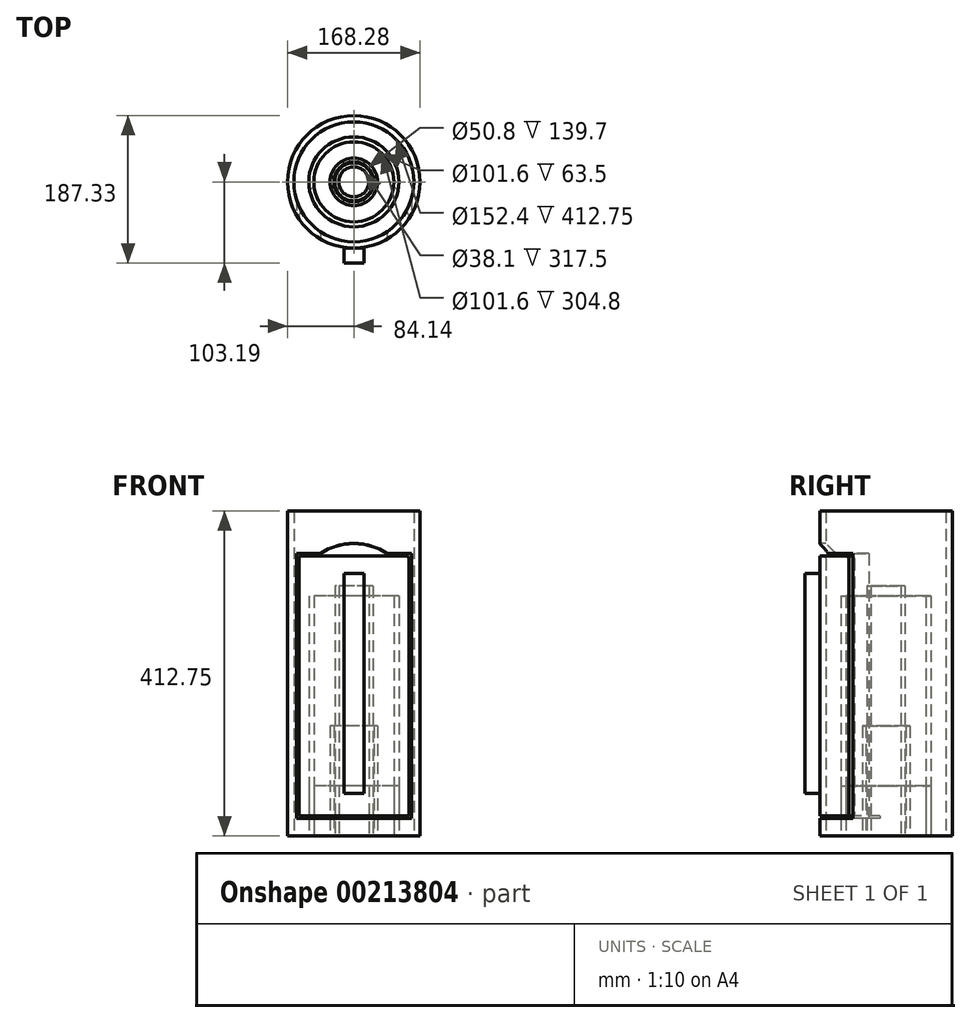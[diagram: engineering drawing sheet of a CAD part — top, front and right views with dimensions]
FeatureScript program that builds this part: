
annotation { "Feature Type Name" : "Feature", "Feature Type Description" : "" }
export const myFeature = defineFeature(function(context is Context, id is Id, definition is map)
    precondition{}
    {
        {
            var Q0;
            Q0=qCreatedBy(makeId("Top.planeOp"),FACE);
            var sketch = newSketch(context, id + "F0", { "sketchPlane" : qUnion([Q0])});
            skCircle(sketch, "E0", {"center": v(0, 0) * mm, "radius": 76.2 * mm});
            skCircle(sketch, "E1", {"center": v(0, 0) * mm, "radius": 84.14 * mm});
            skSolve(sketch);
        }
        {
            var Q0;
            Q0=makeQuery(id+"F0.imprint","IMPRINT",FACE,{"disambiguationData":[TD([[makeQuery(id+"F0.imprint","IMPRINT",EDGE,{"derivedFrom":sQuery(id+"F0.wireOp",EDGE,"E0")}),-1.0]])]});
            extrude(context, id + "F1", {"entities" : qUnion([Q0]), "depth" : 412.75 * mm});
        }
        {
            var Q0;
            Q0=qCreatedBy(makeId("Top.planeOp"),FACE);
            var sketch = newSketch(context, id + "F2", { "sketchPlane" : qUnion([Q0])});
            skCircle(sketch, "E2", {"center": v(0, 0) * mm, "radius": 50.8 * mm});
            skCircle(sketch, "E3", {"center": v(0, 0) * mm, "radius": 57.15 * mm});
            skSolve(sketch);
        }
        {
            var Q0;
            Q0=makeQuery(id+"F2.imprint","IMPRINT",FACE,{"disambiguationData":[TD([[makeQuery(id+"F2.imprint","IMPRINT",EDGE,{"derivedFrom":sQuery(id+"F2.wireOp",EDGE,"E2")}),-1.0]])]});
            extrude(context, id + "F3", {"entities" : qUnion([Q0]), "depth" : 63.5 * mm});
        }
        {
            var Q0;
            Q0=qCreatedBy(makeId("Top.planeOp"),FACE);
            var sketch = newSketch(context, id + "F4", { "sketchPlane" : qUnion([Q0])});
            skCircle(sketch, "E4", {"center": v(0, 0) * mm, "radius": 25.4 * mm});
            skCircle(sketch, "E5", {"center": v(0, 0) * mm, "radius": 30.16 * mm});
            skSolve(sketch);
        }
        {
            var Q0;
            Q0=makeQuery(id+"F4.imprint","IMPRINT",FACE,{"disambiguationData":[TD([[makeQuery(id+"F4.imprint","IMPRINT",EDGE,{"derivedFrom":sQuery(id+"F4.wireOp",EDGE,"E4")}),-1.0]])]});
            extrude(context, id + "F5", {"entities" : qUnion([Q0]), "depth" : 139.7 * mm});
        }
        {
            var Q0;
            Q0 = qSketchRegion(id + "F2", true);
            extrude(context, id + "F6", {"entities" : qUnion([Q0]), "depth" : 304.8 * mm});
        }
        {
            var Q0;
            Q0=qCreatedBy(makeId("Top.planeOp"),FACE);
            var sketch = newSketch(context, id + "F7", { "sketchPlane" : qUnion([Q0])});
            skCircle(sketch, "E6", {"center": v(0, 0) * mm, "radius": 19.05 * mm});
            skCircle(sketch, "E7", {"center": v(0, 0) * mm, "radius": 24.13 * mm});
            skSolve(sketch);
        }
        {
            var Q0;
            Q0=makeQuery(id+"F7.imprint","IMPRINT",FACE,{"disambiguationData":[TD([[makeQuery(id+"F7.imprint","IMPRINT",EDGE,{"derivedFrom":sQuery(id+"F7.wireOp",EDGE,"E6")}),-1.0]])]});
            extrude(context, id + "F8", {"entities" : qUnion([Q0]), "depth" : 317.5 * mm});
        }
        {
            var Q0;
            Q0=qCreatedBy(makeId("Front.planeOp"),FACE);
            cPlane(context, id + "F9", {"entities" : qUnion([Q0]), "cplaneType" : CPlaneType.OFFSET, "offset" : 84.14 * mm, "width" : 152.4 * mm, "height" : 152.4 * mm});
        }
        {
            var Q0;
            Q0=qCreatedBy(id+"F9.planeOp",FACE);
            var sketch = newSketch(context, id + "F10", { "sketchPlane" : qUnion([Q0])});
            skLineSegment(sketch, "E8.bottom", {"start": v(-69.85, 25.4) * mm, "end": v(69.85, 25.4) * mm});
            skLineSegment(sketch, "E8.top", {"start": v(-69.85, 355.6) * mm, "end": v(69.85, 355.6) * mm});
            skLineSegment(sketch, "E8.left", {"start": v(-69.85, 25.4) * mm, "end": v(-69.85, 355.6) * mm});
            skLineSegment(sketch, "E8.right", {"start": v(69.85, 25.4) * mm, "end": v(69.85, 355.6) * mm});
            skLineSegment(sketch, "E9.0", {"start": v(-73.03, 22.23) * mm, "end": v(-73.03, 358.78) * mm});
            skLineSegment(sketch, "E9.1", {"start": v(-73.03, 22.23) * mm, "end": v(73.03, 22.23) * mm});
            skLineSegment(sketch, "E9.2", {"start": v(73.03, 22.23) * mm, "end": v(73.02, 358.78) * mm});
            skLineSegment(sketch, "E9.3", {"start": v(-73.03, 358.78) * mm, "end": v(73.02, 358.78) * mm});
            skSolve(sketch);
        }
        {
            var Q0;
            Q0=makeQuery(id+"F10.imprint","IMPRINT",FACE,{"disambiguationData":[TD([[makeQuery(id+"F10.imprint","IMPRINT",EDGE,{"derivedFrom":sQuery(id+"F10.wireOp",EDGE,"E8.bottom")}),-1.0]])]});
            extrude(context, id + "F11", {"entities" : qUnion([Q0]), "operationType" : NewBodyOperationType.REMOVE, "oppositeDirection" : true, "depth" : 76.2 * mm});
        }
        {
            var Q0;
            Q0=qCreatedBy(id+"F9.planeOp",FACE);
            var sketch = newSketch(context, id + "F12", { "sketchPlane" : qUnion([Q0])});
            skLineSegment(sketch, "E10.0", {"start": v(69.85, 25.4) * mm, "end": v(-69.85, 25.4) * mm});
            skPoint(sketch, "E11", {"position": v(0, 25.4) * mm});
            skSolve(sketch);
        }
        {
            var Q0;
            Q0=makeQuery(id+"F11.boolean.opBoolean","INTERSECT",EDGE,{"derivedFrom":[makeQuery(id+"F1.opExtrude","SWEPT_FACE",FACE,{"disambiguationData":[OSD([sQuery(id+"F0.wireOp",EDGE,"E0")])]}),makeQuery(id+"F11.opExtrude","SWEPT_FACE",FACE,{"disambiguationData":[OSD([sQuery(id+"F10.wireOp",EDGE,"E8.right")])]})]});
            var Q1;
            Q1=makeQuery(id+"F11.boolean.opBoolean","INTERSECT",EDGE,{"derivedFrom":[makeQuery(id+"F1.opExtrude","SWEPT_FACE",FACE,{"disambiguationData":[OSD([sQuery(id+"F0.wireOp",EDGE,"E0")])]}),makeQuery(id+"F11.opExtrude","SWEPT_FACE",FACE,{"disambiguationData":[OSD([sQuery(id+"F10.wireOp",EDGE,"E8.left")])]})]});
            fillet(context, id + "F13", {"entities" : qUnion([Q0, Q1]), "radius" : 3.17 * mm, "tangentPropagation" : true, "allowEdgeOverflow" : false});
        }
        {
            var Q0;
            Q0=makeQuery(id+"F13.opFillet","BLEND_EDGE",EDGE,{"blendedFrom":[makeQuery(id+"F11.boolean.opBoolean","INTERSECT",EDGE,{"derivedFrom":[makeQuery(id+"F1.opExtrude","SWEPT_FACE",FACE,{"disambiguationData":[OSD([sQuery(id+"F0.wireOp",EDGE,"E0")])]}),makeQuery(id+"F11.opExtrude","SWEPT_FACE",FACE,{"disambiguationData":[OSD([sQuery(id+"F10.wireOp",EDGE,"E8.right")])]})]}),makeQuery(id+"F11.boolean.opBoolean","COPY",FACE,{"derivedFrom":makeQuery(id+"F11.opExtrude","SWEPT_FACE",FACE,{"disambiguationData":[OSD([sQuery(id+"F10.wireOp",EDGE,"E8.top")])]})})],"blendedInto":[makeQuery(id+"F11.boolean.opBoolean","COPY",FACE,{"derivedFrom":makeQuery(id+"F11.opExtrude","SWEPT_FACE",FACE,{"disambiguationData":[OSD([sQuery(id+"F10.wireOp",EDGE,"E8.top")])]})})]});
            var Q1;
            Q1=makeQuery(id+"F13.opFillet","BLEND_EDGE",EDGE,{"blendedFrom":[makeQuery(id+"F11.boolean.opBoolean","INTERSECT",EDGE,{"derivedFrom":[makeQuery(id+"F1.opExtrude","SWEPT_FACE",FACE,{"disambiguationData":[OSD([sQuery(id+"F0.wireOp",EDGE,"E0")])]}),makeQuery(id+"F11.opExtrude","SWEPT_FACE",FACE,{"disambiguationData":[OSD([sQuery(id+"F10.wireOp",EDGE,"E8.left")])]})]}),makeQuery(id+"F11.boolean.opBoolean","COPY",FACE,{"derivedFrom":makeQuery(id+"F11.opExtrude","SWEPT_FACE",FACE,{"disambiguationData":[OSD([sQuery(id+"F10.wireOp",EDGE,"E8.top")])]})})],"blendedInto":[makeQuery(id+"F11.boolean.opBoolean","COPY",FACE,{"derivedFrom":makeQuery(id+"F11.opExtrude","SWEPT_FACE",FACE,{"disambiguationData":[OSD([sQuery(id+"F10.wireOp",EDGE,"E8.top")])]})})]});
            fillet(context, id + "F14", {"entities" : qUnion([Q0, Q1]), "radius" : 3.17 * mm, "tangentPropagation" : true, "allowEdgeOverflow" : false});
        }
        {
            var Q0;
            Q0=qCreatedBy(id+"F9.planeOp",FACE);
            var sketch = newSketch(context, id + "F15", { "sketchPlane" : qUnion([Q0])});
            skLineSegment(sketch, "E12.0", {"start": v(73.02, 358.78) * mm, "end": v(-73.03, 358.78) * mm});
            skCircle(sketch, "E13", {"center": v(0, 295.28) * mm, "radius": 76.2 * mm});
            skPoint(sketch, "E13.centerSnap0", {"position": v(0, 358.78) * mm});
            skPoint(sketch, "E14", {"position": v(0, 371.48) * mm});
            skSolve(sketch);
        }
        {
            var Q0;
            {var subQ0=sQuery(id+"F15.wireOp",EDGE,"E13");var subQ1=sQuery(id+"F15.wireOp",EDGE,"E12.0");var subQ2=makeQuery(id+"F15.imprint","INTERSECT",VERTEX,{"disambiguationData":[OD(0.0)],"derivedFrom":[subQ1,subQ0]});Q0=makeQuery(id+"F15.imprint","IMPRINT",FACE,{"disambiguationData":[TD([[makeQuery(id+"F15.imprint","IMPRINT",EDGE,{"disambiguationData":[TD([[subQ2,1.0]])],"derivedFrom":subQ1}),-1.0]])]});}
            extrude(context, id + "F16", {"entities" : qUnion([Q0]), "operationType" : NewBodyOperationType.REMOVE, "oppositeDirection" : true, "depth" : 25.4 * mm});
        }
        {
            var Q0;
            Q0=qCreatedBy(id+"F9.planeOp",FACE);
            var sketch = newSketch(context, id + "F17", { "sketchPlane" : qUnion([Q0])});
            skLineSegment(sketch, "E15.bottom", {"start": v(-12.7, 333.38) * mm, "end": v(12.7, 333.38) * mm});
            skLineSegment(sketch, "E15.top", {"start": v(-12.7, 53.98) * mm, "end": v(12.7, 53.98) * mm});
            skLineSegment(sketch, "E15.left", {"start": v(-12.7, 333.38) * mm, "end": v(-12.7, 53.97) * mm});
            skLineSegment(sketch, "E15.right", {"start": v(12.7, 333.38) * mm, "end": v(12.7, 53.97) * mm});
            skSolve(sketch);
        }
        {
            var Q0;
            Q0=makeQuery(id+"F17.imprint","IMPRINT",FACE,{"disambiguationData":[TD([[makeQuery(id+"F17.imprint","IMPRINT",EDGE,{"derivedFrom":sQuery(id+"F17.wireOp",EDGE,"E15.bottom")}),-1.0]])]});
            extrude(context, id + "F18", {"entities" : qUnion([Q0]), "depth" : 19.05 * mm});
        }
        {
            var Q0;
            Q0=qCreatedBy(id+"F9.planeOp",FACE);
            var sketch = newSketch(context, id + "F19", { "sketchPlane" : qUnion([Q0])});
            skLineSegment(sketch, "E16.0.0", {"start": v(-12.7, 333.38) * mm, "end": v(-12.7, 53.97) * mm, "construction": true});
            skLineSegment(sketch, "E16.0.1", {"start": v(-12.7, 53.98) * mm, "end": v(12.7, 53.98) * mm, "construction": true});
            skLineSegment(sketch, "E16.0.2", {"start": v(12.7, 53.97) * mm, "end": v(12.7, 333.38) * mm, "construction": true});
            skLineSegment(sketch, "E16.0.3", {"start": v(12.7, 333.38) * mm, "end": v(-12.7, 333.38) * mm, "construction": true});
            skLineSegment(sketch, "E17", {"start": v(12.7, 193.68) * mm, "end": v(-12.7, 193.68) * mm, "construction": true});
            skPoint(sketch, "E18", {"position": v(0, 193.68) * mm});
            skSolve(sketch);
        }
    });
